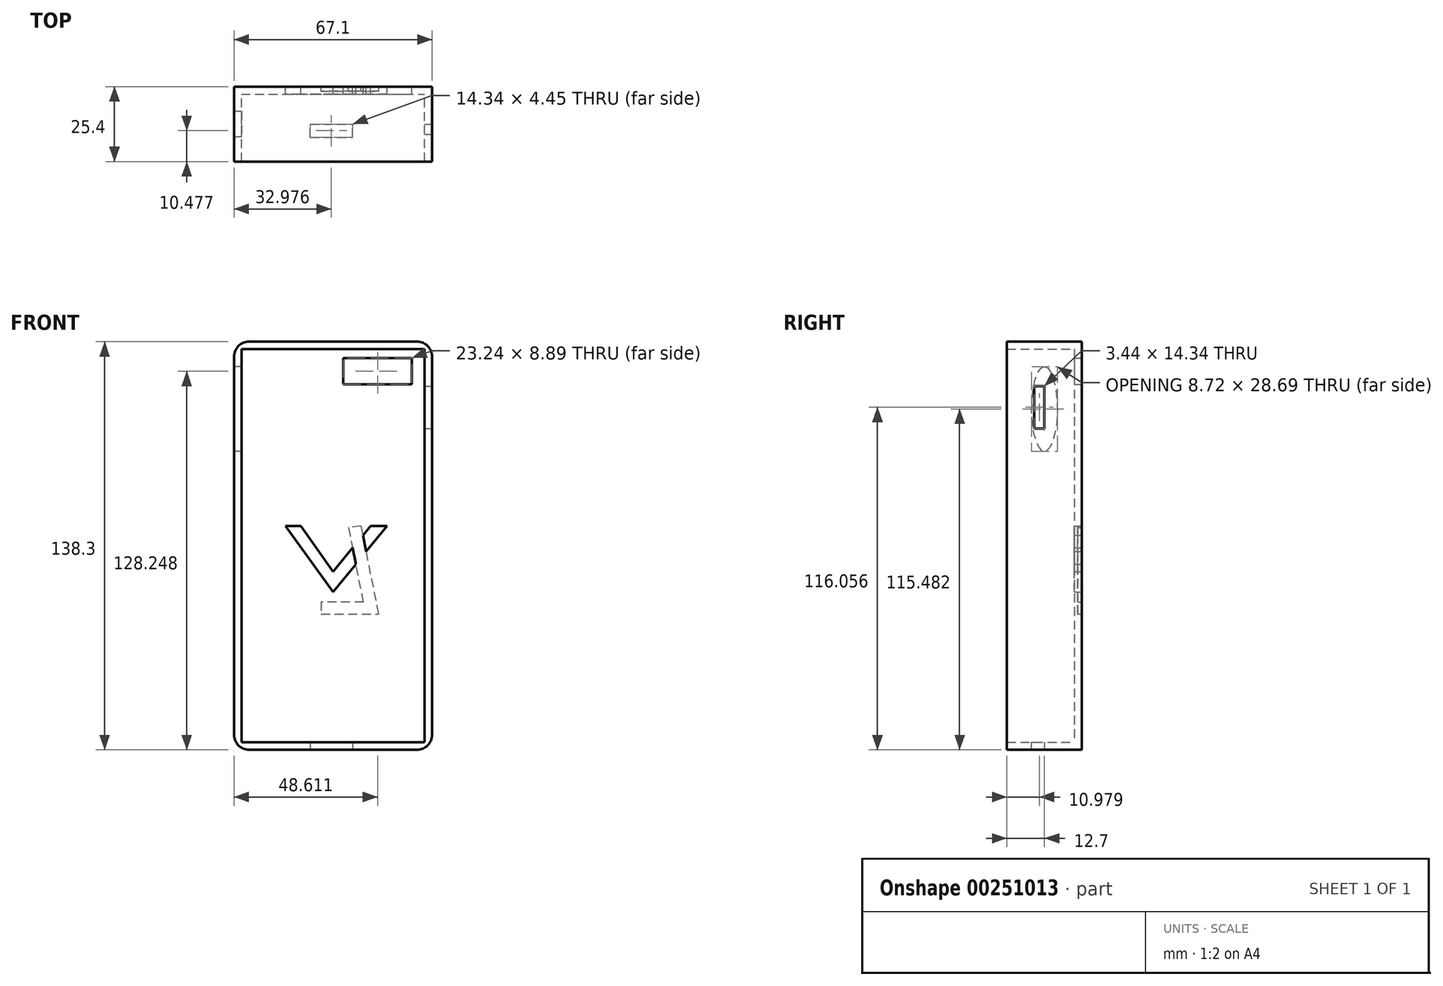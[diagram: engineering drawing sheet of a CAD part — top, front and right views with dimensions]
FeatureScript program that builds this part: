
annotation { "Feature Type Name" : "Feature", "Feature Type Description" : "" }
export const myFeature = defineFeature(function(context is Context, id is Id, definition is map)
    precondition{}
    {
        {
            var Q0;
            Q0=qCreatedBy(makeId("Front.planeOp"),FACE);
            var sketch = newSketch(context, id + "F0", { "sketchPlane" : qUnion([Q0])});
            skLineSegment(sketch, "E0.bottom", {"start": v(-33.55, 69.15) * mm, "end": v(33.55, 69.15) * mm});
            skLineSegment(sketch, "E0.top", {"start": v(-33.55, -69.15) * mm, "end": v(33.55, -69.15) * mm});
            skLineSegment(sketch, "E0.left", {"start": v(-33.55, 69.15) * mm, "end": v(-33.55, -69.15) * mm});
            skLineSegment(sketch, "E0.right", {"start": v(33.55, 69.15) * mm, "end": v(33.55, -69.15) * mm});
            skPoint(sketch, "E0.middle", {"position": v(0, 0) * mm});
            skSolve(sketch);
        }
        {
            var Q0;
            Q0=makeQuery(id+"F0.imprint","IMPRINT",FACE,{"disambiguationData":[TD([[makeQuery(id+"F0.imprint","IMPRINT",EDGE,{"derivedFrom":sQuery(id+"F0.wireOp",EDGE,"E0.bottom")}),-1.0]])]});
            extrude(context, id + "F1", {"entities" : qUnion([Q0]), "endBound" : BoundingType.SYMMETRIC, "depth" : 25.4 * mm});
        }
        {
            var Q0;
            Q0=makeQuery(id+"F1.opExtrude","CAP_FACE",FACE,{"disambiguationData":[OSD([sQuery(id+"F0.wireOp",EDGE,"E0.bottom"),sQuery(id+"F0.wireOp",EDGE,"E0.top"),sQuery(id+"F0.wireOp",EDGE,"E0.left"),sQuery(id+"F0.wireOp",EDGE,"E0.right")])],"isStart":false});
            shell(context, id + "F2", {"entities" : qUnion([Q0]), "thickness" : 2.54 * mm});
        }
        {
            var Q0;
            Q0=makeQuery(id+"F1.opExtrude","SWEPT_EDGE",EDGE,{"disambiguationData":[OSD([sQuery(id+"F0.wireOp",EDGE,"E0.bottom"),sQuery(id+"F0.wireOp",EDGE,"E0.right")])]});
            var Q1;
            Q1=makeQuery(id+"F1.opExtrude","SWEPT_EDGE",EDGE,{"disambiguationData":[OSD([sQuery(id+"F0.wireOp",EDGE,"E0.top"),sQuery(id+"F0.wireOp",EDGE,"E0.right")])]});
            var Q2;
            Q2=makeQuery(id+"F1.opExtrude","SWEPT_EDGE",EDGE,{"disambiguationData":[OSD([sQuery(id+"F0.wireOp",EDGE,"E0.bottom"),sQuery(id+"F0.wireOp",EDGE,"E0.left")])]});
            var Q3;
            Q3=makeQuery(id+"F1.opExtrude","SWEPT_EDGE",EDGE,{"disambiguationData":[OSD([sQuery(id+"F0.wireOp",EDGE,"E0.top"),sQuery(id+"F0.wireOp",EDGE,"E0.left")])]});
            fillet(context, id + "F3", {"entities" : qUnion([Q0, Q1, Q2, Q3]), "radius" : 5.08 * mm, "tangentPropagation" : true, "allowEdgeOverflow" : false});
        }
        {
            var Q0;
            Q0=makeQuery(id+"F2.opShell","OFFSET_FACE",FACE,{"disambiguationData":[OSD([sQuery(id+"F0.wireOp",EDGE,"E0.bottom"),sQuery(id+"F0.wireOp",EDGE,"E0.top"),sQuery(id+"F0.wireOp",EDGE,"E0.left"),sQuery(id+"F0.wireOp",EDGE,"E0.right")])]});
            var sketch = newSketch(context, id + "F4", { "sketchPlane" : qUnion([Q0])});
            skLineSegment(sketch, "E1.bottom", {"start": v(26.68, 54.65) * mm, "end": v(3.44, 54.65) * mm});
            skLineSegment(sketch, "E1.top", {"start": v(26.68, 63.55) * mm, "end": v(3.44, 63.55) * mm});
            skLineSegment(sketch, "E1.left", {"start": v(26.68, 54.65) * mm, "end": v(26.68, 63.55) * mm});
            skLineSegment(sketch, "E1.right", {"start": v(3.44, 54.65) * mm, "end": v(3.44, 63.55) * mm});
            skSolve(sketch);
        }
        {
            var Q0;
            Q0=makeQuery(id+"F4.imprint","IMPRINT",FACE,{"disambiguationData":[TD([[makeQuery(id+"F4.imprint","IMPRINT",EDGE,{"derivedFrom":sQuery(id+"F4.wireOp",EDGE,"E1.bottom")}),-1.0]])]});
            extrude(context, id + "F5", {"entities" : qUnion([Q0]), "operationType" : NewBodyOperationType.REMOVE, "endBound" : BoundingType.SYMMETRIC, "depth" : 25 * mm});
        }
        {
            var Q0;
            Q0=makeQuery(id+"F1.opExtrude","SWEPT_FACE",FACE,{"disambiguationData":[OSD([sQuery(id+"F0.wireOp",EDGE,"E0.top")])]});
            var sketch = newSketch(context, id + "F6", { "sketchPlane" : qUnion([Q0])});
            skLineSegment(sketch, "E2.bottom", {"start": v(6.6, 0) * mm, "end": v(-7.75, 0) * mm});
            skLineSegment(sketch, "E2.top", {"start": v(6.6, 4.45) * mm, "end": v(-7.75, 4.45) * mm});
            skLineSegment(sketch, "E2.left", {"start": v(6.6, 0) * mm, "end": v(6.6, 4.45) * mm});
            skLineSegment(sketch, "E2.right", {"start": v(-7.75, 0) * mm, "end": v(-7.75, 4.45) * mm});
            skSolve(sketch);
        }
        {
            var Q0;
            Q0=makeQuery(id+"F6.imprint","IMPRINT",FACE,{"disambiguationData":[TD([[makeQuery(id+"F6.imprint","IMPRINT",EDGE,{"derivedFrom":sQuery(id+"F6.wireOp",EDGE,"E2.bottom")}),-1.0]])]});
            extrude(context, id + "F7", {"entities" : qUnion([Q0]), "operationType" : NewBodyOperationType.REMOVE, "endBound" : BoundingType.SYMMETRIC, "oppositeDirection" : true, "depth" : 70 * mm});
        }
        {
            var Q0;
            Q0=makeQuery(id+"F1.opExtrude","SWEPT_FACE",FACE,{"disambiguationData":[OSD([sQuery(id+"F0.wireOp",EDGE,"E0.left")])]});
            var sketch = newSketch(context, id + "F8", { "sketchPlane" : qUnion([Q0])});
            skEllipse(sketch, "E3", {"center": v(0, 46.33) * mm, "majorRadius": 14.34 * mm, "minorRadius": 4.36 * mm, "majorAxis": v(0, 1)});
            skSolve(sketch);
        }
        {
            var Q0;
            Q0=makeQuery(id+"F8.imprint","IMPRINT",FACE,{"disambiguationData":[TD([[makeQuery(id+"F8.imprint","IMPRINT",EDGE,{"derivedFrom":sQuery(id+"F8.wireOp",EDGE,"E3")}),1.0]])]});
            extrude(context, id + "F9", {"entities" : qUnion([Q0]), "operationType" : NewBodyOperationType.REMOVE, "endBound" : BoundingType.SYMMETRIC, "oppositeDirection" : true, "depth" : 55 * mm});
        }
        {
            var Q0;
            Q0=makeQuery(id+"F1.opExtrude","SWEPT_FACE",FACE,{"disambiguationData":[OSD([sQuery(id+"F0.wireOp",EDGE,"E0.right")])]});
            var sketch = newSketch(context, id + "F10", { "sketchPlane" : qUnion([Q0])});
            skLineSegment(sketch, "E4.bottom", {"start": v(-3.44, 39.73) * mm, "end": v(0, 39.73) * mm});
            skLineSegment(sketch, "E4.top", {"start": v(-3.44, 54.08) * mm, "end": v(0, 54.08) * mm});
            skLineSegment(sketch, "E4.left", {"start": v(-3.44, 39.73) * mm, "end": v(-3.44, 54.08) * mm});
            skLineSegment(sketch, "E4.right", {"start": v(0, 39.73) * mm, "end": v(0, 54.08) * mm});
            skSolve(sketch);
        }
        {
            var Q0;
            Q0=makeQuery(id+"F10.imprint","IMPRINT",FACE,{"disambiguationData":[TD([[makeQuery(id+"F10.imprint","IMPRINT",EDGE,{"derivedFrom":sQuery(id+"F10.wireOp",EDGE,"E4.bottom")}),1.0]])]});
            extrude(context, id + "F11", {"entities" : qUnion([Q0]), "operationType" : NewBodyOperationType.REMOVE, "endBound" : BoundingType.SYMMETRIC, "oppositeDirection" : true, "depth" : 55 * mm});
        }
        {
            var Q0;
            Q0=makeQuery(id+"F1.opExtrude","CAP_FACE",FACE,{"disambiguationData":[OSD([sQuery(id+"F0.wireOp",EDGE,"E0.bottom"),sQuery(id+"F0.wireOp",EDGE,"E0.top"),sQuery(id+"F0.wireOp",EDGE,"E0.left"),sQuery(id+"F0.wireOp",EDGE,"E0.right")])],"isStart":true});
            var sketch = newSketch(context, id + "F12", { "sketchPlane" : qUnion([Q0])});
            skLineSegment(sketch, "E5", {"start": v(-9.47, 6.74) * mm, "end": v(-15.5, -23.1) * mm});
            skLineSegment(sketch, "E6", {"start": v(-15.5, -23.1) * mm, "end": v(4.02, -23.1) * mm});
            skLineSegment(sketch, "E7", {"start": v(4.02, -23.1) * mm, "end": v(4.02, -19.08) * mm});
            skLineSegment(sketch, "E8", {"start": v(4.02, -19.08) * mm, "end": v(-10.33, -19.08) * mm});
            skLineSegment(sketch, "E9", {"start": v(-10.33, -19.08) * mm, "end": v(-5.24, 6.13) * mm});
            skLineSegment(sketch, "E10", {"start": v(-5.24, 6.13) * mm, "end": v(-9.47, 6.74) * mm});
            skSolve(sketch);
        }
        {
            var Q0;
            Q0=makeQuery(id+"F12.imprint","IMPRINT",FACE,{"disambiguationData":[TD([[makeQuery(id+"F12.imprint","IMPRINT",EDGE,{"derivedFrom":sQuery(id+"F12.wireOp",EDGE,"E5")}),1.0]])]});
            extrude(context, id + "F13", {"entities" : qUnion([Q0]), "operationType" : NewBodyOperationType.REMOVE, "endBound" : BoundingType.SYMMETRIC, "oppositeDirection" : true, "depth" : 3 * mm});
        }
        {
            var Q0;
            Q0=makeQuery(id+"F1.opExtrude","CAP_FACE",FACE,{"disambiguationData":[OSD([sQuery(id+"F0.wireOp",EDGE,"E0.bottom"),sQuery(id+"F0.wireOp",EDGE,"E0.top"),sQuery(id+"F0.wireOp",EDGE,"E0.left"),sQuery(id+"F0.wireOp",EDGE,"E0.right")])],"isStart":true});
            var sketch = newSketch(context, id + "F14", { "sketchPlane" : qUnion([Q0])});
            skLineSegment(sketch, "E11", {"start": v(-18.36, 6.74) * mm, "end": v(0, -15.64) * mm});
            skLineSegment(sketch, "E12", {"start": v(0, -15.64) * mm, "end": v(16.07, 6.74) * mm});
            skLineSegment(sketch, "E13", {"start": v(16.07, 6.74) * mm, "end": v(10.9, 6.74) * mm});
            skLineSegment(sketch, "E14", {"start": v(10.9, 6.74) * mm, "end": v(0, -8.75) * mm});
            skLineSegment(sketch, "E15", {"start": v(0, -8.75) * mm, "end": v(-12.71, 6.74) * mm});
            skLineSegment(sketch, "E16", {"start": v(-12.71, 6.74) * mm, "end": v(-18.36, 6.74) * mm});
            skSolve(sketch);
        }
        {
            var Q0;
            {var subQ0=sQuery(id+"F14.wireOp",EDGE,"E16");Q0=makeQuery(id+"F14.imprint","IMPRINT",FACE,{"disambiguationData":[TD([[makeQuery(id+"F14.imprint","IMPRINT",EDGE,{"derivedFrom":subQ0}),1.0]])]});}
            var Q1;
            {var subQ0=sQuery(id+"F14.wireOp",EDGE,"E12");Q1=makeQuery(id+"F14.imprint","IMPRINT",FACE,{"disambiguationData":[TD([[makeQuery(id+"F14.imprint","IMPRINT",EDGE,{"derivedFrom":subQ0}),1.0]])]});}
            extrude(context, id + "F15", {"entities" : qUnion([Q0, Q1]), "operationType" : NewBodyOperationType.REMOVE, "endBound" : BoundingType.SYMMETRIC, "oppositeDirection" : true, "depth" : 55 * mm});
        }
    });
